# Revit family: CT1134A SINGLE LEVER STOP VALVE
name_source: partatom
category: Plumbing Fixtures
revit_build: Autodesk Revit 2017 (Build: 20160225_1515(x64)
units: mm (PartAtom-declared; Revit-internal decimal feet)

## family parameters
Always vertical = Yes
Cut with Voids When Loaded = No
Part Type = Normal
Room Calculation Point = No
Round Connector Dimension = Use Diameter
Shared = No
Work Plane-Based = No

## types (1)
- CT1134A SINGLE LEVER STOP VALVE
    CW Connection = No
    Drain = 0 mm  [stored 0 ft]
    Manufacturer = COTTO
    Material = SCG เซรามิก
    Standard = มอก.792-2554
    Waste Connection = No
    Water Supply = 0 mm  [stored 0 ft]
    กว้าง (มม.) = 0 mm  [stored 0 ft]
    ยาว (มม.) = 0 mm  [stored 0 ft]
    สูง (มม.) = 0 mm  [stored 0 ft]

note: [stored X ft] marks values corroborated as IEEE doubles in the binary element streams (Revit-internal decimal feet)

## geometry (parser evidence)
native form markers: Sweep x3
no freeform markers — native parametric forms only
